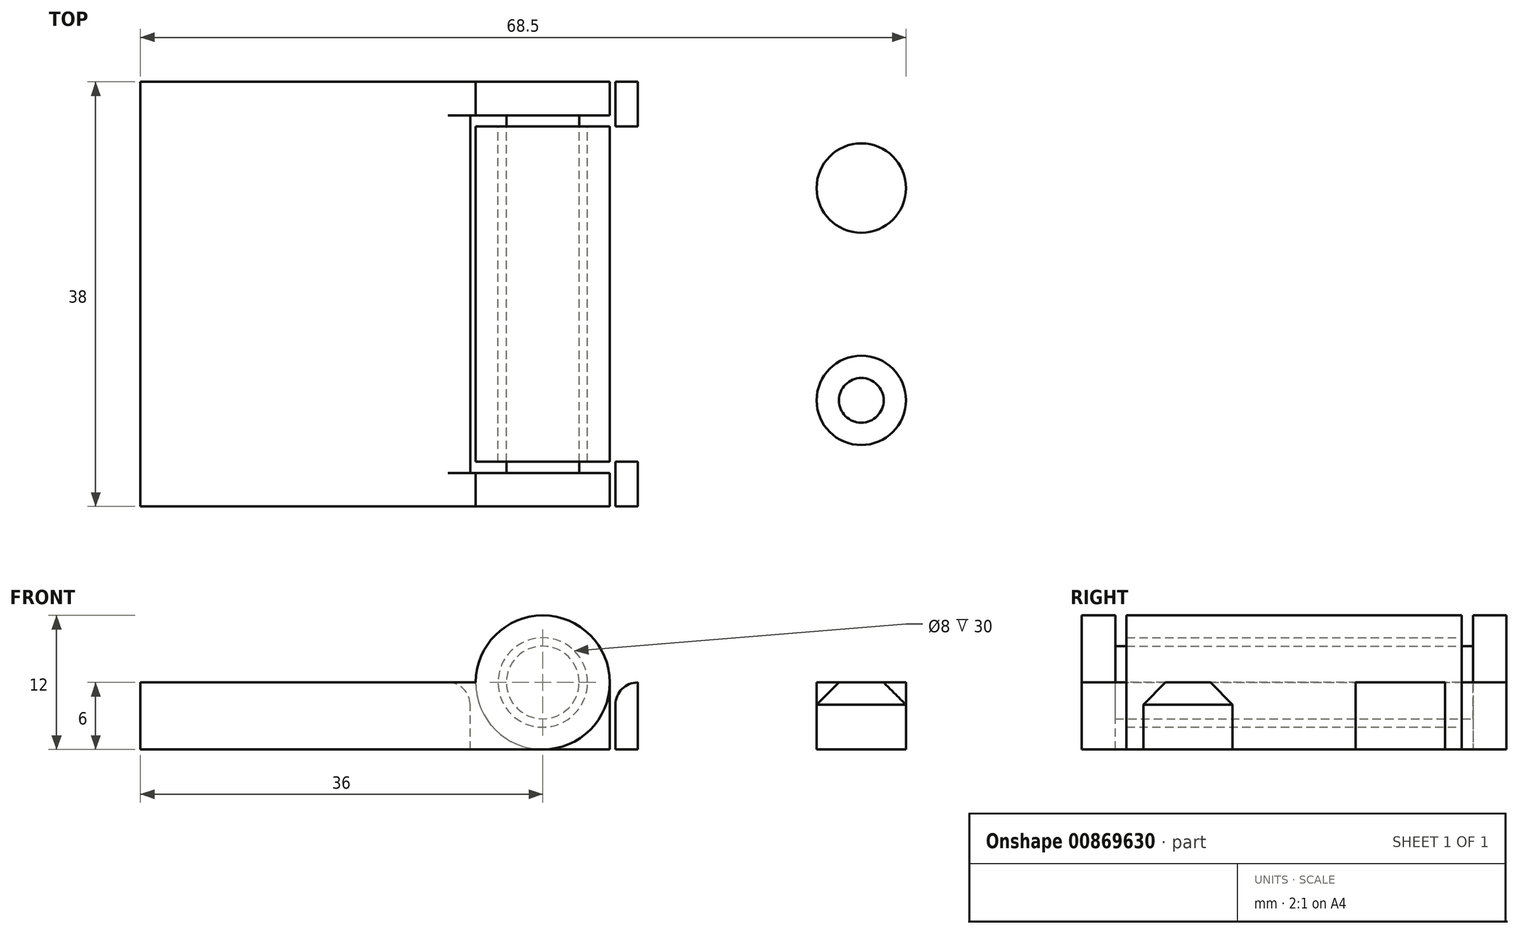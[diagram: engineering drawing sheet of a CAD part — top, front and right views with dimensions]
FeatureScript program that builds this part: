
annotation { "Feature Type Name" : "Feature", "Feature Type Description" : "" }
export const myFeature = defineFeature(function(context is Context, id is Id, definition is map)
    precondition{}
    {
        {
            var Q0;
            Q0=qCreatedBy(makeId("Front.planeOp"),FACE);
            var sketch = newSketch(context, id + "F0", { "sketchPlane" : qUnion([Q0])});
            skLineSegment(sketch, "E0.bottom", {"start": v(0, 0) * mm, "end": v(30, 0) * mm});
            skLineSegment(sketch, "E0.top", {"start": v(0, 6) * mm, "end": v(30, 6) * mm});
            skLineSegment(sketch, "E0.left", {"start": v(0, 0) * mm, "end": v(0, 6) * mm});
            skLineSegment(sketch, "E0.right", {"start": v(30, 0) * mm, "end": v(30, 6) * mm});
            skCircle(sketch, "E1", {"center": v(-6, 6) * mm, "radius": 6 * mm});
            skLineSegment(sketch, "E2", {"start": v(0, 0) * mm, "end": v(-6, 0) * mm});
            skLineSegment(sketch, "E3", {"start": v(-6, 6) * mm, "end": v(-6, 0) * mm});
            skCircle(sketch, "E4", {"center": v(-6, 6) * mm, "radius": 4 * mm});
            skCircle(sketch, "E5", {"center": v(-6, 6) * mm, "radius": 3.25 * mm});
            skSolve(sketch);
        }
        {
            var Q0;
            Q0=makeQuery(id+"F0.imprint","IMPRINT",FACE,{"disambiguationData":[TD([[makeQuery(id+"F0.imprint","IMPRINT",EDGE,{"derivedFrom":sQuery(id+"F0.wireOp",EDGE,"E0.bottom")}),1.0]])]});
            var Q1;
            {var subQ0=sQuery(id+"F0.wireOp",EDGE,"E0.left");Q1=makeQuery(id+"F0.imprint","IMPRINT",FACE,{"disambiguationData":[TD([[makeQuery(id+"F0.imprint","IMPRINT",EDGE,{"derivedFrom":subQ0}),1.0]])]});}
            var Q2;
            Q2=makeQuery(id+"F0.imprint","IMPRINT",FACE,{"disambiguationData":[TD([[makeQuery(id+"F0.imprint","IMPRINT",EDGE,{"derivedFrom":sQuery(id+"F0.wireOp",EDGE,"E4")}),-1.0]])]});
            var Q3;
            Q3=makeQuery(id+"F0.imprint","IMPRINT",FACE,{"disambiguationData":[TD([[makeQuery(id+"F0.imprint","IMPRINT",EDGE,{"derivedFrom":sQuery(id+"F0.wireOp",EDGE,"E5")}),1.0]])]});
            extrude(context, id + "F1", {"entities" : qUnion([Q0, Q1, Q2, Q3]), "endBound" : BoundingType.SYMMETRIC, "depth" : 30 * mm, "offsetDistance" : 25 * mm});
        }
        {
            var Q0;
            Q0=makeQuery(id+"F1.opExtrude","CAP_FACE",FACE,{"disambiguationData":[OSD([sQuery(id+"F0.wireOp",EDGE,"E5")])],"isStart":false});
            var Q1;
            Q1=makeQuery(id+"F1.opExtrude","CAP_FACE",FACE,{"disambiguationData":[OSD([sQuery(id+"F0.wireOp",EDGE,"E5")])],"isStart":true});
            extrude(context, id + "F2", {"entities" : qUnion([Q0, Q1]), "operationType" : NewBodyOperationType.ADD, "depth" : 1 * mm, "offsetDistance" : 25 * mm, "hasSecondDirection" : true, "secondDirectionOppositeDirection" : true, "secondDirectionDepth" : 1 * mm});
        }
        {
            var Q0;
            {var subQ0=sQuery(id+"F0.wireOp",EDGE,"E5");Q0=makeQuery(id+"F2.opExtrude","CAP_FACE",FACE,{"disambiguationData":[OSD([subQ0]),TDD([makeQuery(id+"F1.opExtrude","CAP_FACE",FACE,{"disambiguationData":[OSD([subQ0])],"isStart":false})])],"isStart":false});}
            var sketch = newSketch(context, id + "F3", { "sketchPlane" : qUnion([Q0])});
            skLineSegment(sketch, "E6", {"start": v(-6, 6) * mm, "end": v(-6, 0) * mm});
            skLineSegment(sketch, "E7", {"start": v(-6, 0) * mm, "end": v(0, 0) * mm});
            skCircle(sketch, "E8", {"center": v(-6, 6) * mm, "radius": 6 * mm});
            skLineSegment(sketch, "E9", {"start": v(-6, 0) * mm, "end": v(-42, 0) * mm});
            skLineSegment(sketch, "E10", {"start": v(-42, 0) * mm, "end": v(-42, 6) * mm});
            skLineSegment(sketch, "E11", {"start": v(-42, 6) * mm, "end": v(-6, 6) * mm});
            skSolve(sketch);
        }
        {
            var Q0;
            Q0 = qSketchRegion(id + "F3", true);
            extrude(context, id + "F4", {"entities" : qUnion([Q0]), "operationType" : NewBodyOperationType.ADD, "depth" : 3 * mm, "offsetDistance" : 25 * mm});
        }
        {
            var Q0;
            {var subQ0=sQuery(id+"F0.wireOp",EDGE,"E5");Q0=makeQuery(id+"F2.opExtrude","CAP_FACE",FACE,{"disambiguationData":[OSD([subQ0]),TDD([makeQuery(id+"F1.opExtrude","CAP_FACE",FACE,{"disambiguationData":[OSD([subQ0])],"isStart":true})])],"isStart":true});}
            var sketch = newSketch(context, id + "F5", { "sketchPlane" : qUnion([Q0])});
            skCircle(sketch, "E12", {"center": v(6, 6) * mm, "radius": 6 * mm});
            skLineSegment(sketch, "E13", {"start": v(6, 6) * mm, "end": v(6, 0) * mm});
            skLineSegment(sketch, "E14", {"start": v(6, 0) * mm, "end": v(42, 0) * mm});
            skLineSegment(sketch, "E15", {"start": v(42, 0) * mm, "end": v(42, 6) * mm});
            skLineSegment(sketch, "E16", {"start": v(42, 6) * mm, "end": v(6, 6) * mm});
            skSolve(sketch);
        }
        {
            var Q0;
            Q0 = qSketchRegion(id + "F5", true);
            extrude(context, id + "F6", {"entities" : qUnion([Q0]), "operationType" : NewBodyOperationType.ADD, "depth" : 3 * mm, "offsetDistance" : 25 * mm});
        }
        {
            var Q0;
            Q0=makeQuery(id+"F4.opExtrude","CAP_FACE",FACE,{"disambiguationData":[OSD([sQuery(id+"F3.wireOp",EDGE,"E8"),sQuery(id+"F3.wireOp",EDGE,"E9"),sQuery(id+"F3.wireOp",EDGE,"E10"),sQuery(id+"F3.wireOp",EDGE,"E11")])],"isStart":true});
            var sketch = newSketch(context, id + "F7", { "sketchPlane" : qUnion([Q0])});
            skLineSegment(sketch, "E17.bottom", {"start": v(42, 0) * mm, "end": v(12.5, 0) * mm});
            skLineSegment(sketch, "E17.top", {"start": v(42, 6) * mm, "end": v(12.5, 6) * mm});
            skLineSegment(sketch, "E17.left", {"start": v(42, 0) * mm, "end": v(42, 6) * mm});
            skLineSegment(sketch, "E17.right", {"start": v(12.5, 0) * mm, "end": v(12.5, 6) * mm});
            skLineSegment(sketch, "E18", {"start": v(12.5, 0) * mm, "end": v(8.5, 0) * mm});
            skLineSegment(sketch, "E19", {"start": v(12.5, 6) * mm, "end": v(12, 6) * mm});
            skSolve(sketch);
        }
        {
            var Q0;
            Q0=makeQuery(id+"F7.imprint","IMPRINT",FACE,{"disambiguationData":[TD([[makeQuery(id+"F7.imprint","IMPRINT",EDGE,{"derivedFrom":sQuery(id+"F7.wireOp",EDGE,"E17.bottom")}),1.0]])]});
            extrude(context, id + "F8", {"entities" : qUnion([Q0]), "operationType" : NewBodyOperationType.ADD, "depth" : 34 * mm, "offsetDistance" : 25 * mm});
        }
        {
            var Q0;
            Q0=makeQuery(id+"F1.opExtrude","CAP_FACE",FACE,{"disambiguationData":[OSD([sQuery(id+"F0.wireOp",EDGE,"E0.bottom"),sQuery(id+"F0.wireOp",EDGE,"E0.top"),sQuery(id+"F0.wireOp",EDGE,"E0.right"),sQuery(id+"F0.wireOp",EDGE,"E1"),sQuery(id+"F0.wireOp",EDGE,"E2"),sQuery(id+"F0.wireOp",EDGE,"E4")])],"isStart":true});
            var sketch = newSketch(context, id + "F9", { "sketchPlane" : qUnion([Q0])});
            skLineSegment(sketch, "E20.bottom", {"start": v(-30, 0) * mm, "end": v(-0.5, 0) * mm});
            skLineSegment(sketch, "E20.top", {"start": v(-30, 6) * mm, "end": v(-0.5, 6) * mm});
            skLineSegment(sketch, "E20.left", {"start": v(-30, 0) * mm, "end": v(-30, 6) * mm});
            skLineSegment(sketch, "E20.right", {"start": v(-0.5, 0) * mm, "end": v(-0.5, 6) * mm});
            skLineSegment(sketch, "E21", {"start": v(-0.5, 6) * mm, "end": v(0, 6) * mm});
            skSolve(sketch);
        }
        {
            var Q0;
            Q0=makeQuery(id+"F9.imprint","IMPRINT",FACE,{"disambiguationData":[TD([[makeQuery(id+"F9.imprint","IMPRINT",EDGE,{"derivedFrom":sQuery(id+"F9.wireOp",EDGE,"E20.bottom")}),-1.0]])]});
            extrude(context, id + "F10", {"entities" : qUnion([Q0]), "operationType" : NewBodyOperationType.ADD, "depth" : 4 * mm, "offsetDistance" : 25 * mm, "hasSecondDirection" : true, "secondDirectionOppositeDirection" : true, "secondDirectionDepth" : 34 * mm});
        }
        {
            var Q0;
            Q0=makeQuery(id+"F8.opExtrude","SWEPT_EDGE",EDGE,{"disambiguationData":[OSD([sQuery(id+"F7.wireOp",EDGE,"E17.top"),sQuery(id+"F7.wireOp",EDGE,"E17.right"),sQuery(id+"F7.wireOp",EDGE,"E19")])]});
            var Q1;
            {var subQ0=sQuery(id+"F9.wireOp",EDGE,"E20.right");var subQ1=sQuery(id+"F9.wireOp",EDGE,"E20.top");Q1=makeQuery(id+"F10.boolean.opBoolean","SPLIT",EDGE,{"disambiguationData":[TD([makeQuery(id+"F10.opExtrude","CAP_FACE",FACE,{"disambiguationData":[OSD([sQuery(id+"F9.wireOp",EDGE,"E20.bottom"),subQ1,sQuery(id+"F9.wireOp",EDGE,"E20.left"),subQ0])],"isStart":false})])],"derivedFrom":makeQuery(id+"F10.opExtrude","SWEPT_EDGE",EDGE,{"disambiguationData":[OSD([subQ1,subQ0,sQuery(id+"F9.wireOp",EDGE,"E21")])]})});}
            var Q2;
            {var subQ0=sQuery(id+"F9.wireOp",EDGE,"E20.top");var subQ1=sQuery(id+"F9.wireOp",EDGE,"E20.right");Q2=makeQuery(id+"F10.boolean.opBoolean","SPLIT",EDGE,{"disambiguationData":[TD([makeQuery(id+"F10.opExtrude","CAP_FACE",FACE,{"disambiguationData":[OSD([sQuery(id+"F9.wireOp",EDGE,"E20.bottom"),subQ0,sQuery(id+"F9.wireOp",EDGE,"E20.left"),subQ1])],"isStart":true})])],"derivedFrom":makeQuery(id+"F10.opExtrude","SWEPT_EDGE",EDGE,{"disambiguationData":[OSD([subQ0,subQ1,sQuery(id+"F9.wireOp",EDGE,"E21")])]})});}
            fillet(context, id + "F11", {"entities" : qUnion([Q0, Q1, Q2]), "radius" : 2 * mm, "tangentPropagation" : true, "allowEdgeOverflow" : false});
        }
        {
            var Q0;
            Q0=makeQuery(id+"F10.boolean.opBoolean","MERGE",FACE,{"derivedFrom":[makeQuery(id+"F1.opExtrude","SWEPT_FACE",FACE,{"disambiguationData":[OSD([sQuery(id+"F0.wireOp",EDGE,"E0.top")])]}),makeQuery(id+"F10.opExtrude","SWEPT_FACE",FACE,{"disambiguationData":[OSD([sQuery(id+"F9.wireOp",EDGE,"E20.top")])]})]});
            var sketch = newSketch(context, id + "F12", { "sketchPlane" : qUnion([Q0])});
            skLineSegment(sketch, "E22", {"start": v(0, 0) * mm, "end": v(30, 0) * mm});
            skLineSegment(sketch, "E23", {"start": v(15, 0) * mm, "end": v(30, 19) * mm});
            skLineSegment(sketch, "E24", {"start": v(15, 0) * mm, "end": v(30, -19) * mm});
            skCircle(sketch, "E25", {"center": v(9, 0) * mm, "radius": 4 * mm});
            skCircle(sketch, "E26", {"center": v(22.5, 9.5) * mm, "radius": 4 * mm});
            skCircle(sketch, "E27", {"center": v(22.5, -9.5) * mm, "radius": 4 * mm});
            skLineSegment(sketch, "E28", {"start": v(0, 0) * mm, "end": v(-6, 0) * mm});
            skLineSegment(sketch, "E29", {"start": v(-6, 0) * mm, "end": v(-6, 5.68) * mm});
            skCircle(sketch, "E30.MirrorC", {"center": v(-21, 0) * mm, "radius": 4 * mm});
            skCircle(sketch, "E31.MirrorC", {"center": v(-34.5, 9.5) * mm, "radius": 4 * mm});
            skCircle(sketch, "E32.MirrorC", {"center": v(-34.5, -9.5) * mm, "radius": 4 * mm});
            skLineSegment(sketch, "E33.MirrorCS", {"start": v(-27, 0) * mm, "end": v(-42, 19) * mm});
            skLineSegment(sketch, "E34.MirrorCS", {"start": v(-27, 0) * mm, "end": v(-42, -19) * mm});
            skLineSegment(sketch, "E35", {"start": v(9, 0) * mm, "end": v(15, 0) * mm});
            skSolve(sketch);
        }
        {
            var Q0;
            {var subQ0=sQuery(id+"F12.wireOp",EDGE,"E33.MirrorCS");var subQ1=sQuery(id+"F12.wireOp",EDGE,"E31.MirrorC");var subQ2=makeQuery(id+"F12.imprint","INTERSECT",VERTEX,{"disambiguationData":[OD(0.0)],"derivedFrom":[subQ1,subQ0]});Q0=makeQuery(id+"F12.imprint","IMPRINT",FACE,{"disambiguationData":[TD([[makeQuery(id+"F12.imprint","IMPRINT",EDGE,{"disambiguationData":[TD([[subQ2,-1.0]])],"derivedFrom":subQ1}),-1.0]])]});}
            var Q1;
            {var subQ0=sQuery(id+"F12.wireOp",EDGE,"E33.MirrorCS");var subQ1=sQuery(id+"F12.wireOp",EDGE,"E31.MirrorC");var subQ2=makeQuery(id+"F12.imprint","INTERSECT",VERTEX,{"disambiguationData":[OD(0.0)],"derivedFrom":[subQ1,subQ0]});Q1=makeQuery(id+"F12.imprint","IMPRINT",FACE,{"disambiguationData":[TD([[makeQuery(id+"F12.imprint","IMPRINT",EDGE,{"disambiguationData":[TD([[subQ2,1.0]])],"derivedFrom":subQ1}),-1.0]])]});}
            var Q2;
            {var subQ0=sQuery(id+"F12.wireOp",EDGE,"E34.MirrorCS");var subQ1=sQuery(id+"F12.wireOp",EDGE,"E32.MirrorC");var subQ2=makeQuery(id+"F12.imprint","INTERSECT",VERTEX,{"disambiguationData":[OD(0.0)],"derivedFrom":[subQ1,subQ0]});Q2=makeQuery(id+"F12.imprint","IMPRINT",FACE,{"disambiguationData":[TD([[makeQuery(id+"F12.imprint","IMPRINT",EDGE,{"disambiguationData":[TD([[subQ2,1.0]])],"derivedFrom":subQ1}),-1.0]])]});}
            var Q3;
            {var subQ0=sQuery(id+"F12.wireOp",EDGE,"E34.MirrorCS");var subQ1=sQuery(id+"F12.wireOp",EDGE,"E32.MirrorC");var subQ2=makeQuery(id+"F12.imprint","INTERSECT",VERTEX,{"disambiguationData":[OD(0.0)],"derivedFrom":[subQ1,subQ0]});Q3=makeQuery(id+"F12.imprint","IMPRINT",FACE,{"disambiguationData":[TD([[makeQuery(id+"F12.imprint","IMPRINT",EDGE,{"disambiguationData":[TD([[subQ2,-1.0]])],"derivedFrom":subQ1}),-1.0]])]});}
            var Q4;
            Q4=makeQuery(id+"F12.imprint","IMPRINT",FACE,{"disambiguationData":[TD([[makeQuery(id+"F12.imprint","IMPRINT",EDGE,{"derivedFrom":sQuery(id+"F12.wireOp",EDGE,"E30.MirrorC")}),-1.0]])]});
            var Q5;
            {var subQ0=sQuery(id+"F12.wireOp",EDGE,"G6lh3tvB-ETin-aIgi-hxeT-IoEbUMC0h2qv");var subQ1=sQuery(id+"F12.wireOp",EDGE,"pHL4QKsS-bjJP-J5fH-yabG-gqUfOWPNrpg6");var subQ2=makeQuery(id+"F12.imprint","INTERSECT",VERTEX,{"derivedFrom":[subQ1,subQ0]});Q5=makeQuery(id+"F12.imprint","IMPRINT",FACE,{"disambiguationData":[TD([[makeQuery(id+"F12.imprint","IMPRINT",EDGE,{"disambiguationData":[TD([[subQ2,1.0]])],"derivedFrom":subQ1}),1.0]])]});}
            var Q6;
            {var subQ0=sQuery(id+"F12.wireOp",EDGE,"G6lh3tvB-ETin-aIgi-hxeT-IoEbUMC0h2qv");var subQ1=sQuery(id+"F12.wireOp",EDGE,"pHL4QKsS-bjJP-J5fH-yabG-gqUfOWPNrpg6");var subQ2=makeQuery(id+"F12.imprint","INTERSECT",VERTEX,{"derivedFrom":[subQ1,subQ0]});Q6=makeQuery(id+"F12.imprint","IMPRINT",FACE,{"disambiguationData":[TD([[makeQuery(id+"F12.imprint","IMPRINT",EDGE,{"disambiguationData":[TD([[subQ2,1.0]])],"derivedFrom":subQ1}),-1.0]])]});}
            var Q7;
            {var subQ0=sQuery(id+"F12.wireOp",EDGE,"E27");var subQ1=sQuery(id+"F12.wireOp",EDGE,"E24");var subQ2=makeQuery(id+"F12.imprint","INTERSECT",VERTEX,{"disambiguationData":[OD(0.0)],"derivedFrom":[subQ1,subQ0]});Q7=makeQuery(id+"F12.imprint","IMPRINT",FACE,{"disambiguationData":[TD([[makeQuery(id+"F12.imprint","IMPRINT",EDGE,{"disambiguationData":[TD([[subQ2,-1.0]])],"derivedFrom":subQ1}),-1.0]])]});}
            var Q8;
            {var subQ0=sQuery(id+"F12.wireOp",EDGE,"E27");var subQ1=sQuery(id+"F12.wireOp",EDGE,"E24");var subQ2=makeQuery(id+"F12.imprint","INTERSECT",VERTEX,{"disambiguationData":[OD(0.0)],"derivedFrom":[subQ1,subQ0]});Q8=makeQuery(id+"F12.imprint","IMPRINT",FACE,{"disambiguationData":[TD([[makeQuery(id+"F12.imprint","IMPRINT",EDGE,{"disambiguationData":[TD([[subQ2,-1.0]])],"derivedFrom":subQ1}),1.0]])]});}
            var Q9;
            {var subQ0=sQuery(id+"F12.wireOp",EDGE,"E26");var subQ1=sQuery(id+"F12.wireOp",EDGE,"E23");var subQ2=makeQuery(id+"F12.imprint","INTERSECT",VERTEX,{"disambiguationData":[OD(0.0)],"derivedFrom":[subQ1,subQ0]});Q9=makeQuery(id+"F12.imprint","IMPRINT",FACE,{"disambiguationData":[TD([[makeQuery(id+"F12.imprint","IMPRINT",EDGE,{"disambiguationData":[TD([[subQ2,-1.0]])],"derivedFrom":subQ1}),-1.0]])]});}
            var Q10;
            {var subQ0=sQuery(id+"F12.wireOp",EDGE,"E26");var subQ1=sQuery(id+"F12.wireOp",EDGE,"E23");var subQ2=makeQuery(id+"F12.imprint","INTERSECT",VERTEX,{"disambiguationData":[OD(0.0)],"derivedFrom":[subQ1,subQ0]});Q10=makeQuery(id+"F12.imprint","IMPRINT",FACE,{"disambiguationData":[TD([[makeQuery(id+"F12.imprint","IMPRINT",EDGE,{"disambiguationData":[TD([[subQ2,-1.0]])],"derivedFrom":subQ1}),1.0]])]});}
            var Q11;
            {var subQ0=sQuery(id+"F12.wireOp",EDGE,"E35");var subQ1=sQuery(id+"F12.wireOp",EDGE,"E22");var subQ2=makeQuery(id+"F12.imprint","INTERSECT",VERTEX,{"derivedFrom":[subQ1,subQ0]});Q11=makeQuery(id+"F12.imprint","IMPRINT",FACE,{"disambiguationData":[TD([[makeQuery(id+"F12.imprint","IMPRINT",EDGE,{"disambiguationData":[TD([[subQ2,1.0]])],"derivedFrom":subQ1}),-1.0]])]});}
            var Q12;
            {var subQ0=sQuery(id+"F12.wireOp",EDGE,"E35");var subQ1=sQuery(id+"F12.wireOp",EDGE,"E22");var subQ2=makeQuery(id+"F12.imprint","INTERSECT",VERTEX,{"derivedFrom":[subQ1,subQ0]});Q12=makeQuery(id+"F12.imprint","IMPRINT",FACE,{"disambiguationData":[TD([[makeQuery(id+"F12.imprint","IMPRINT",EDGE,{"disambiguationData":[TD([[subQ2,1.0]])],"derivedFrom":subQ1}),1.0]])]});}
            extrude(context, id + "F13", {"entities" : qUnion([Q0, Q1, Q2, Q3, Q4, Q5, Q6, Q7, Q8, Q9, Q10, Q11, Q12]), "operationType" : NewBodyOperationType.REMOVE, "oppositeDirection" : true, "depth" : 25 * mm, "offsetDistance" : 25 * mm});
        }
        {
            var Q0;
            Q0=makeQuery(id+"F13.boolean.opBoolean","COPY",EDGE,{"derivedFrom":makeQuery(id+"F13.opExtrude","CAP_EDGE",EDGE,{"disambiguationData":[OSD([sQuery(id+"F12.wireOp",EDGE,"E31.MirrorC")])],"isStart":true})});
            var Q1;
            Q1=makeQuery(id+"F13.boolean.opBoolean","COPY",EDGE,{"derivedFrom":makeQuery(id+"F13.opExtrude","CAP_EDGE",EDGE,{"disambiguationData":[OSD([sQuery(id+"F12.wireOp",EDGE,"E30.MirrorC")])],"isStart":true})});
            var Q2;
            Q2=makeQuery(id+"F13.boolean.opBoolean","COPY",EDGE,{"derivedFrom":makeQuery(id+"F13.opExtrude","CAP_EDGE",EDGE,{"disambiguationData":[OSD([sQuery(id+"F12.wireOp",EDGE,"E32.MirrorC")])],"isStart":true})});
            var Q3;
            Q3=makeQuery(id+"F13.boolean.opBoolean","COPY",EDGE,{"derivedFrom":makeQuery(id+"F13.opExtrude","CAP_EDGE",EDGE,{"disambiguationData":[OSD([sQuery(id+"F12.wireOp",EDGE,"E25")])],"isStart":true})});
            var Q4;
            Q4=makeQuery(id+"F13.boolean.opBoolean","COPY",EDGE,{"derivedFrom":makeQuery(id+"F13.opExtrude","CAP_EDGE",EDGE,{"disambiguationData":[OSD([sQuery(id+"F12.wireOp",EDGE,"E27")])],"isStart":true})});
            var Q5;
            Q5=makeQuery(id+"F13.boolean.opBoolean","COPY",EDGE,{"derivedFrom":makeQuery(id+"F13.opExtrude","CAP_EDGE",EDGE,{"disambiguationData":[OSD([sQuery(id+"F12.wireOp",EDGE,"E26")])],"isStart":true})});
            chamfer(context, id + "F14", {"entities" : qUnion([Q0, Q1, Q2, Q3, Q4, Q5]), "width" : 2 * mm, "tangentPropagation" : true});
        }
    });
